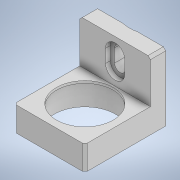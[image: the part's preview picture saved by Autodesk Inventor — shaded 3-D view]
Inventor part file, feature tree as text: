
AUTODESK INVENTOR PART (.ipt)
format: ipt  version: 2020 (Build 240168000, 168)  size: 305,664 bytes
history: native  units: in
note: dims shown in document units (in); Inventor stores cm internally (conversion verified against a paired STEP export)
features: extrude x8, sketch x7, other x2, hole x1, chamfer x1
ambient origin geometry x8: Origin, YZ Plane, XZ Plane, XY Plane, X Axis, Y Axis, Z Axis, Center Point
bodies: Body1 (feature_tree)
feature tree (19):
  other  "ADAPTER_SM1"
  other  "Table"
  extrude  "Extrusion3"  Depth=0.5807in
  extrude  "Extrusion4"  Depth=0.252in TaperAngle=0.0deg
  sketch  "Sketch7"  dims[d31=0.0in d32=0.0in]
  sketch  "Sketch9"  dims[d33=0.0in d34=0.0in]
  extrude  "Extrusion6"  TaperAngle=0.0deg  [1 undecoded]
  hole  "Hole3"  [1 undecoded]
  extrude  "Extrusion7"  Depth=0.0827in TaperAngle=0.0deg
  extrude  "Extrusion8"  Depth=0.3622in TaperAngle=0.0deg
  extrude  "Extrusion9"  TaperAngle=0.0deg  [1 undecoded]
  extrude  "Extrusion10"  Depth=0.3937in
  chamfer  "Chamfer10"  Distance=0.3622in
  extrude  "Extrusion11"  Depth=0.3937in TaperAngle=0.0deg
  sketch  "Sketch4"  dims[d24=1.1102in d26=0.5807in]
  sketch  "Sketch5"  dims[d28=0.4016in d29=0.252in d30=0.0in]
  sketch  "Sketch10"  dims[d35=1.0787in d36=0.0in d77=0.0827in d78=0.0in]
  sketch  "Sketch11"  dims[d85=0.0827in d86=0.328in d87=0.297in d88=0.11in d89=90.0deg d90=0.0827in d91=0.0in d93=0.3622in d94=0.0in]
  sketch  "Sketch13"  dims[d96=0.0in d97=0.0in d98=0.9331in d99=0.3622in d100=0.0in d131=0.3543in d134=0.1727in d135=0.0in d136=0.315in d137=0.315in d138=0.0in d139=0.2165in d140=0.0in d141=0.1083in d142=0.3543in d143=0.1728in d144=0.0in d183=0.7087in d185=0.0886in d186=0.2165in d187=0.0in d188=0.3543in d189=0.0413in d190=0.0392in d191=0.0in d192=0.1969in d193=0.0394in d194=0.0787in d195=45.0deg d196=0.0in d197=1.0in d198=0.7382in d199=0.3937in d200=0.0in d201=0.75in d202=0.5807in]
note: 3 required parameter values undecoded (feature->parameter linkage not recoverable at this tier; creation-order binding heuristic only, values carry confidence <= 0.55)
